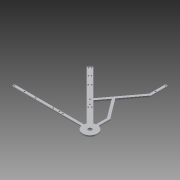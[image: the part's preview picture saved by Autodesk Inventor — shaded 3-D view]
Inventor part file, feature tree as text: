
AUTODESK INVENTOR PART (.ipt)
format: ipt  version: 2013 (Build 170138000, 138)  size: 219,648 bytes
history: native  units: in
note: dims shown in document units (in); Inventor stores cm internally (conversion verified against a paired STEP export)
features: extrude x5, sketch x5, reference x5, projected_geometry x1
ambient origin geometry x8: Origin, YZ Plane, XZ Plane, XY Plane, X Axis, Y Axis, Z Axis, Center Point
bodies: Solid1 (feature_tree)
feature tree (16):
  extrude  "Extrusion1"  Depth=0.25in TaperAngle=0.0deg
  extrude  "Extrusion6"  Depth=0.25in TaperAngle=0.0deg
  extrude  "Extrusion7"  TaperAngle=0.0deg  [1 undecoded]
  extrude  "Extrusion8"  Depth=1.0in TaperAngle=0.0deg
  extrude  "Extrusion9"  Depth=0.25in TaperAngle=0.0deg
  sketch  "Sketch1"  dims[d2=0.5in d3=0.5in d4=1.5in d6=1.5in d7=0.25in d8=0.25in d9=0.25in d10=0.5in d11=0.5in d12=3.75in d13=0.266in d14=0.266in d15=0.266in d16=0.25in d17=0.266in d18=0.25in d19=0.25in d20=0.266in d21=0.266in d22=0.266in d23=0.25in d24=0.266in d25=1.125in d28=1.5in d30=0.25in d31=5.5in d34=0.25in d37=10.926in d38=10.6389in d39=0.2871in d40=0.2871in d41=15.5in d42=15.5in d43=0.25in d44=0.5in d45=0.266in d46=0.25in d47=0.266in d48=0.266in d49=15.5in d50=0.25in d51=0.266in d52=0.25in d54=0.266in d55=0.266in d56=0.266in d57=2.0in d58=2.0in d59=2.0in d60=0.297in d61=0.297in d62=0.297in d63=0.297in d64=2.0in d67=0.25in d68=0.0in]
  sketch  "Sketch7"  dims[d99=0.748in d100=0.25in d101=0.0in]
  sketch  "Sketch9"  dims[d102=0.0in d103=0.0in]
  reference  "Reference6"
  sketch  "Sketch10"  dims[d104=0.0in d105=1.0in d106=0.0in]
  projected_geometry  "Projected Loop2"
  sketch  "Sketch11"  dims[d107=0.5in d109=0.25in d110=0.0in d111=1.0in d112=0.0in]
  reference  "Reference7"
  reference  "Reference8"
  reference  "Reference9"
  reference  "Reference10"
note: 1 required parameter value undecoded (feature->parameter linkage not recoverable at this tier; creation-order binding heuristic only, values carry confidence <= 0.55)
